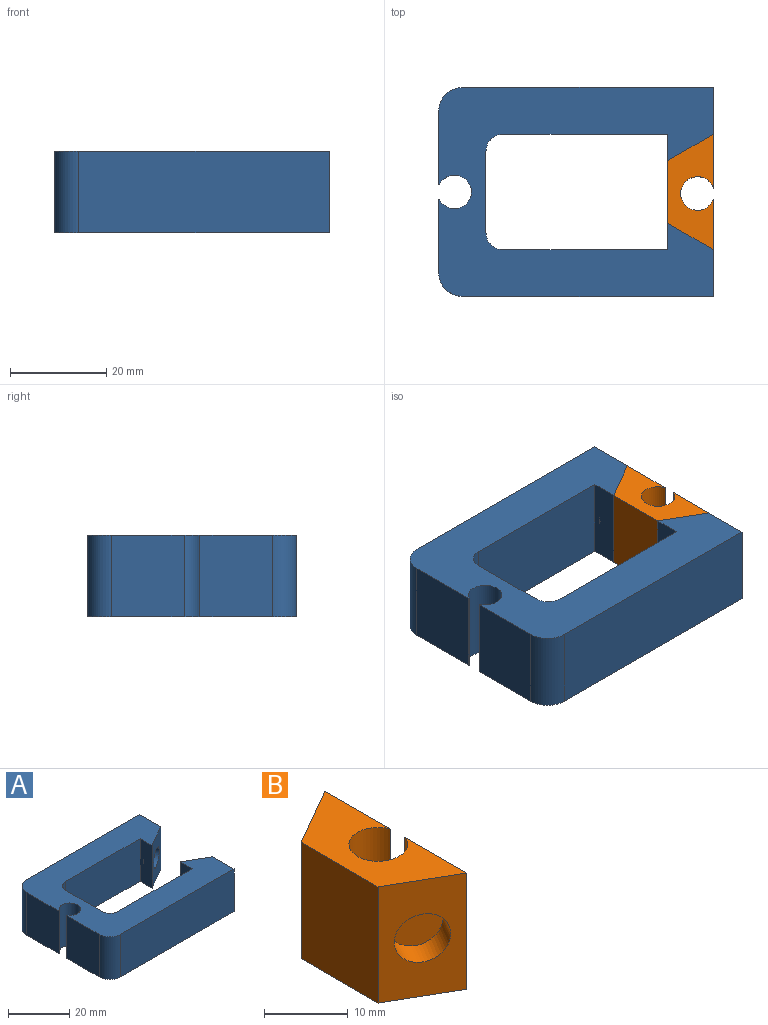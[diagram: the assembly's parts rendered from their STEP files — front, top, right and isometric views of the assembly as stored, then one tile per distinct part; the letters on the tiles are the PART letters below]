
ASSEMBLY  parts=2 mates=1
PART A: 26 faces, bbox 57.1x43.5x17 mm
  f0: plane 34.26x17mm, normal (0,-1,0), area 582.4mm2, adj f1,f14,f15,f17
  f1: plane 17x5.5mm, normal (-1,0,0), area 93.5mm2, adj f0,f2,f14,f15,f22,f23
  f2: plane 17x9.53mm, normal (0.5,-0.87,0), area 148.5mm2, adj f1,f3,f14,f15,f23
  f3: plane 17x9.72mm, normal (1,0,0), area 165.3mm2, adj f2,f4,f14,f15
  f4: plane 52.12x17mm, normal (0,1,0), area 886.1mm2, adj f3,f14,f15,f18
  f5: plane 17x15.08mm, normal (-1,0,0), area 256.3mm2, adj f14,f15,f18,f20
  f6: cylinder r=3.5mm len=17mm, axis (0,0,-1), area 317.4mm2, adj f14,f15,f20,f21
  f7: plane 17x15.08mm, normal (-1,0,0), area 256.3mm2, adj f14,f15,f19,f21
  f8: plane 52.12x17mm, normal (0,-1,0), area 886.1mm2, adj f9,f14,f15,f19
  f9: plane 17x9.72mm, normal (1,0,0), area 165.3mm2, adj f8,f10,f14,f15
  f10: plane 17x9.53mm, normal (0.5,0.87,0), area 148.5mm2, adj f9,f11,f14,f15,f24
  f11: plane 17.02x5.52mm, normal (-1,0,0), area 93.5mm2, adj f10,f12,f14,f15,f24,f25
  f12: plane 34.26x17mm, normal (0,1,0), area 582.4mm2, adj f11,f14,f15,f16
  f13: plane 17x17mm, normal (1,0,0), area 289mm2, adj f14,f15,f16,f17
  f14: plane 57.12x43.44mm, normal (0,0,1), area 1355.3mm2, adj f0,f1,f2,f3,f4,f5,f6,f7
  f15: plane 57.12x43.44mm, normal (0,0,-1), area 1355.3mm2, adj f0,f1,f2,f3,f4,f5,f6,f7
  f16: cylinder r=3.5mm len=17mm, axis (0,0,1), area 93.5mm2, adj f12,f13,f14,f15
  f17: cylinder r=3.5mm len=17mm, axis (0,0,-1), area 93.5mm2, adj f0,f13,f14,f15
  f18: cylinder r=5mm len=17mm, axis (0,0,-1), area 133.5mm2, adj f4,f5,f14,f15
  f19: cylinder r=5mm len=17mm, axis (0,0,-1), area 133.5mm2, adj f7,f8,f14,f15
  f20: cylinder r=0.1mm len=17mm, axis (0,0,-1), area 4.5mm2, adj f5,f6,f14,f15
  f21: cylinder r=0.1mm len=17mm, axis (0,0,-1), area 4.5mm2, adj f6,f7,f14,f15
  f22: plane 7x6.04mm, normal (0.5,-0.87,0), area 38.5mm2, adj f1,f23
  f23: cylinder r=3.5mm len=7.81mm, axis (0.5,-0.87,0), area 77mm2, adj f1,f2,f22
  f24: cylinder r=3.5mm len=7.81mm, axis (0.5,0.87,0), area 77mm2, adj f10,f11,f25
  f25: plane 7x6.04mm, normal (0.5,0.87,0), area 38.5mm2, adj f11,f24
PART B: 12 faces, bbox 9.6x24x17 mm
  f0: plane 17x9.53mm, normal (-0.5,0.87,0), area 148.5mm2, adj f1,f5,f6,f7,f8
  f1: plane 17x13mm, normal (-1,0,0), area 221mm2, adj f0,f2,f6,f7
  f2: plane 17x9.53mm, normal (-0.5,-0.87,0), area 148.5mm2, adj f1,f3,f6,f7,f10
  f3: plane 17.02x10.53mm, normal (1,0,0), area 178.8mm2, adj f2,f4,f6,f7,f10,f11
  f4: cylinder r=3.5mm len=17mm, axis (0,0,-1), area 333.6mm2, adj f3,f5,f6,f7
  f5: plane 17x11.16mm, normal (1,0,0), area 189.7mm2, adj f0,f4,f6,f7,f8,f9
  f6: plane 24x9.53mm, normal (0,0,1), area 138.1mm2, adj f0,f1,f2,f3,f4,f5
  f7: plane 24x9.53mm, normal (0,0,-1), area 138.1mm2, adj f0,f1,f2,f3,f4,f5
  f8: cylinder r=3.5mm len=7.81mm, axis (-0.5,0.87,0), area 77mm2, adj f0,f5,f9
  f9: plane 7x6.04mm, normal (-0.5,0.87,0), area 38.5mm2, adj f5,f8
  f10: cylinder r=3.5mm len=7.81mm, axis (-0.5,-0.87,0), area 77mm2, adj f2,f3,f11
  f11: plane 7x6.04mm, normal (-0.5,-0.87,0), area 38.5mm2, adj f3,f10
PLACE A t=(7.16,0.08,-0.01)mm
PLACE B t=(9.42,8.79,-0.01)mm
MATE planar A.f10 <-> B.f2  axis (0.5,0.87,0) through (16.46,-6.42,8.49)mm
